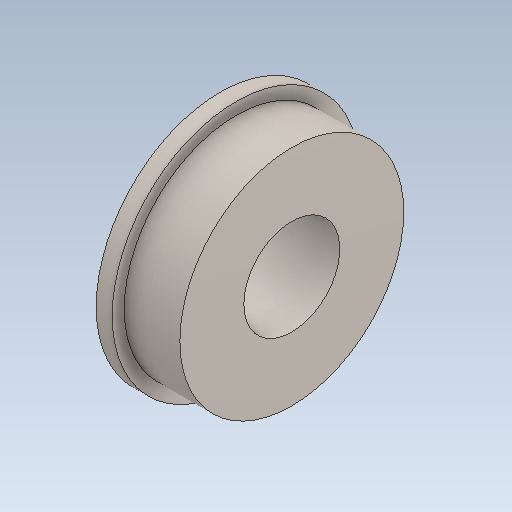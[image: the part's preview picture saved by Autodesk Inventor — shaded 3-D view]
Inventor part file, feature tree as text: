
AUTODESK INVENTOR PART (.ipt)
format: ipt  version: 2020 (Build 240168000, 168)  size: 137,216 bytes
history: native  units: in
note: dims shown in document units (in); Inventor stores cm internally (conversion verified against a paired STEP export)
features: revolve x1
ambient origin geometry x8: Origin, YZ Plane, XZ Plane, XY Plane, X Axis, Y Axis, Z Axis, Center Point
bodies: Solid1 (feature_tree)
feature tree (1):
  revolve  "Revolve1"  [1 undecoded]
note: 1 required parameter value undecoded (feature->parameter linkage not recoverable at this tier; creation-order binding heuristic only, values carry confidence <= 0.55)
